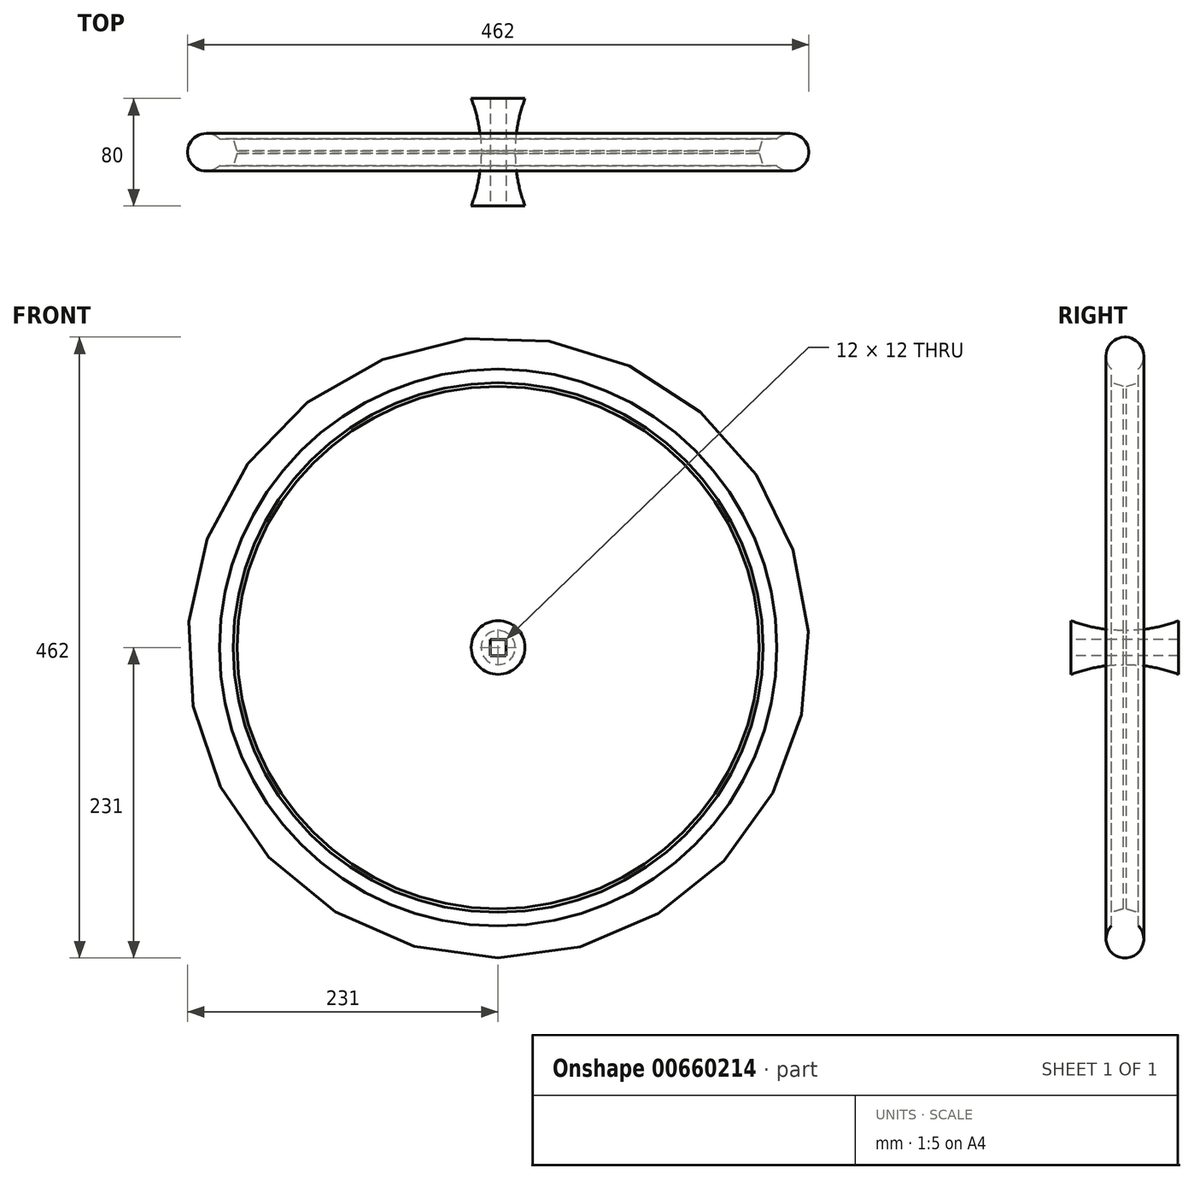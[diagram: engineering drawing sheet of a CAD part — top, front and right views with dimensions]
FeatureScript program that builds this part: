
annotation { "Feature Type Name" : "Feature", "Feature Type Description" : "" }
export const myFeature = defineFeature(function(context is Context, id is Id, definition is map)
    precondition{}
    {
        {
            var Q0;
            Q0=qCreatedBy(makeId("Right.planeOp"),FACE);
            var sketch = newSketch(context, id + "F0", { "sketchPlane" : qUnion([Q0])});
            skArc(sketch, "E0", {"start": v(10, 207.2) * mm, "mid": v(0, 231) * mm, "end": v(-10, 207.2) * mm});
            skLineSegment(sketch, "E1.left", {"start": v(-10, 197) * mm, "end": v(-10, 207.2) * mm});
            skLineSegment(sketch, "E1.right", {"start": v(10, 197) * mm, "end": v(10, 207.2) * mm});
            skLineSegment(sketch, "E2", {"start": v(-10, 197) * mm, "end": v(-1, 194.3) * mm});
            skLineSegment(sketch, "E3", {"start": v(1, 194.3) * mm, "end": v(10, 197) * mm});
            skPoint(sketch, "E1.bottom.end.orphan", {"position": v(0, 197) * mm});
            skLineSegment(sketch, "E4", {"start": v(-23.85, 0) * mm, "end": v(27.38, 0) * mm, "construction": true});
            skLineSegment(sketch, "E5.top", {"start": v(-40, 0) * mm, "end": v(40, 0) * mm});
            skLineSegment(sketch, "E5.left", {"start": v(-40, 20) * mm, "end": v(-40, 0) * mm});
            skLineSegment(sketch, "E5.right", {"start": v(40, 20) * mm, "end": v(40, 10) * mm});
            skArc(sketch, "E6", {"start": v(-40, 20) * mm, "mid": v(-20.83, 14.6) * mm, "end": v(-1, 12.66) * mm});
            skLineSegment(sketch, "E7.bottom", {"start": v(40, 0) * mm, "end": v(40, 0) * mm});
            skLineSegment(sketch, "E7.top", {"start": v(40, 10) * mm, "end": v(40, 10) * mm});
            skLineSegment(sketch, "E7.right", {"start": v(40, 0) * mm, "end": v(40, 10) * mm});
            skLineSegment(sketch, "E8.left", {"start": v(-1, 194.3) * mm, "end": v(-1, 12.66) * mm});
            skLineSegment(sketch, "E8.right", {"start": v(1, 194.3) * mm, "end": v(1, 12.66) * mm});
            skArc(sketch, "E9.trimOffspring", {"start": v(1, 12.66) * mm, "mid": v(20.83, 14.6) * mm, "end": v(40, 20) * mm});
            skSolve(sketch);
        }
        {
            var Q0;
            Q0=makeQuery(id+"F0.imprint","IMPRINT",FACE,{"disambiguationData":[TD([[makeQuery(id+"F0.imprint","IMPRINT",EDGE,{"derivedFrom":sQuery(id+"F0.wireOp",EDGE,"E0")}),1.0]])]});
            var Q1;
            Q1=makeQuery(id+"F0.imprint","IMPRINT",FACE,{"disambiguationData":[TD([[makeQuery(id+"F0.imprint","IMPRINT",EDGE,{"derivedFrom":sQuery(id+"F0.wireOp",EDGE,"E5.top")}),1.0]])]});
            var Q2;
            Q2=sQuery(id+"F0.wireOp",EDGE,"E4");
            revolve(context, id + "F1", {"surfaceOperationType" : NewSurfaceOperationType.NEW, "entities" : qUnion([Q0, Q1]), "axis" : qUnion([Q2]), "revolveType" : RevolveType.FULL});
        }
        {
            var Q0;
            Q0=makeQuery(id+"F1.opRevolve","SWEPT_FACE",FACE,{"disambiguationData":[OSD([sQuery(id+"F0.wireOp",EDGE,"E5.left")])]});
            var sketch = newSketch(context, id + "F2", { "sketchPlane" : qUnion([Q0])});
            skLineSegment(sketch, "E10.bottom", {"start": v(-6, 6) * mm, "end": v(6, 6) * mm});
            skLineSegment(sketch, "E10.top", {"start": v(-6, -6) * mm, "end": v(6, -6) * mm});
            skLineSegment(sketch, "E10.left", {"start": v(-6, 6) * mm, "end": v(-6, -6) * mm});
            skLineSegment(sketch, "E10.right", {"start": v(6, 6) * mm, "end": v(6, -6) * mm});
            skSolve(sketch);
        }
        {
            var Q0;
            Q0 = qSketchRegion(id + "F2", true);
            extrude(context, id + "F3", {"entities" : qUnion([Q0]), "operationType" : NewBodyOperationType.REMOVE, "endBound" : BoundingType.THROUGH_ALL, "oppositeDirection" : true, "depth" : 25 * mm, "offsetDistance" : 25 * mm});
        }
    });
